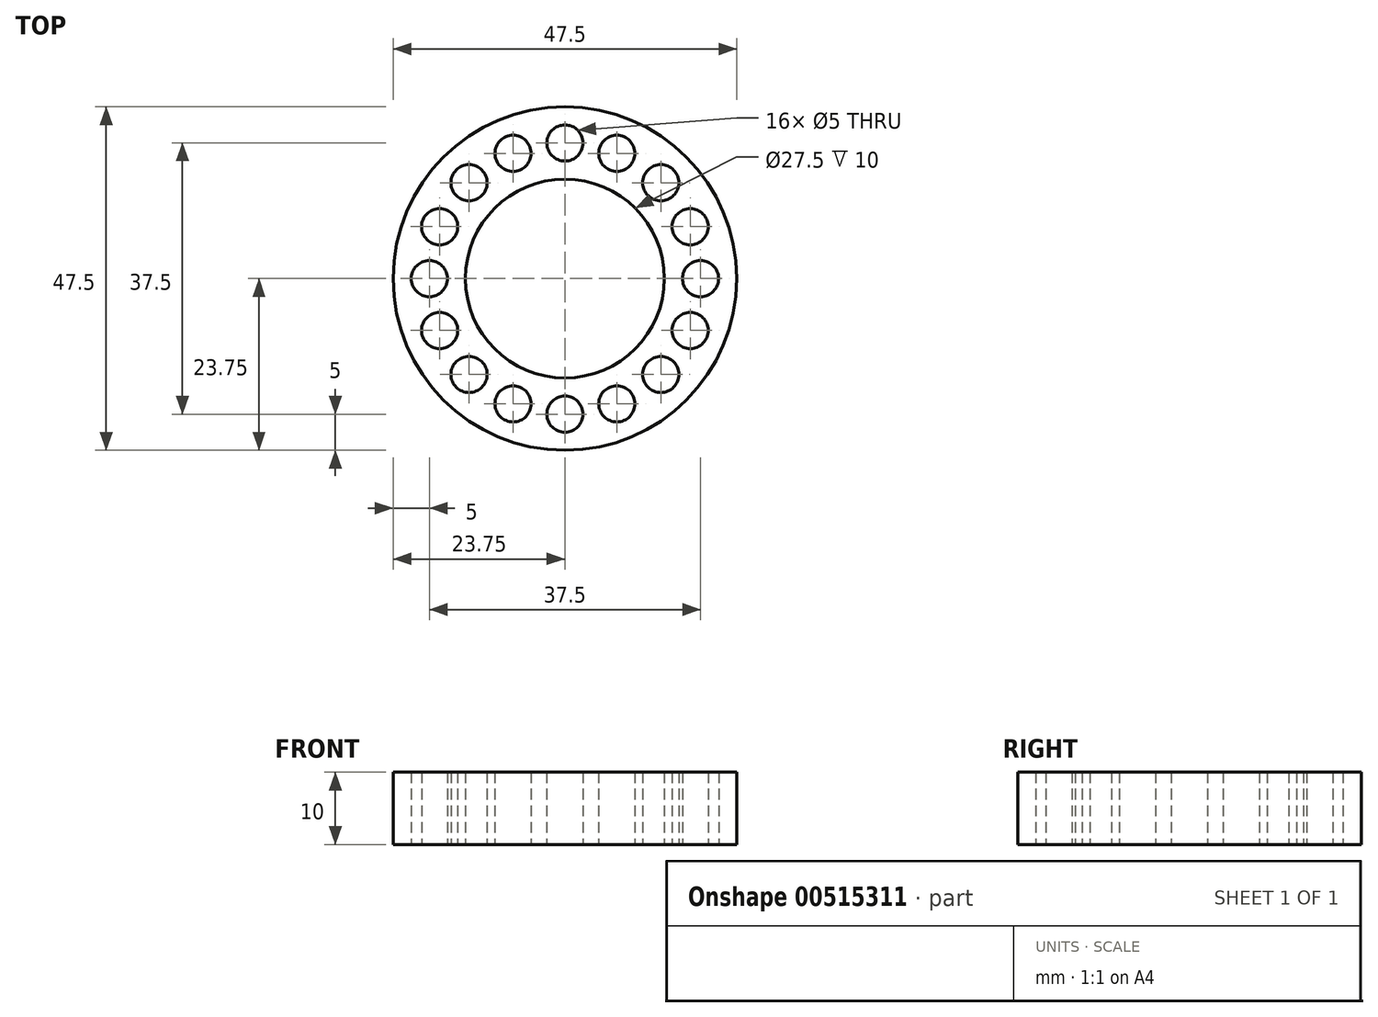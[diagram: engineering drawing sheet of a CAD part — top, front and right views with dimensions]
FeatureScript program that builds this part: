
annotation { "Feature Type Name" : "Feature", "Feature Type Description" : "" }
export const myFeature = defineFeature(function(context is Context, id is Id, definition is map)
    precondition{}
    {
        {
            var Q0;
            Q0=qCreatedBy(makeId("Top.planeOp"),FACE);
            var sketch = newSketch(context, id + "F0", { "sketchPlane" : qUnion([Q0])});
            skCircle(sketch, "E0", {"center": v(0, 0) * mm, "radius": 23.75 * mm});
            skCircle(sketch, "E1", {"center": v(0, 0) * mm, "radius": 13.75 * mm});
            skCircle(sketch, "E2", {"center": v(-13.26, 13.26) * mm, "radius": 2.5 * mm});
            skCircle(sketch, "E3", {"center": v(-18.75, 0) * mm, "radius": 2.5 * mm});
            skCircle(sketch, "E4", {"center": v(-13.26, -13.26) * mm, "radius": 2.5 * mm});
            skCircle(sketch, "E5", {"center": v(0, -18.75) * mm, "radius": 2.5 * mm});
            skCircle(sketch, "E6", {"center": v(13.26, -13.26) * mm, "radius": 2.5 * mm});
            skCircle(sketch, "E7", {"center": v(18.75, 0) * mm, "radius": 2.5 * mm});
            skCircle(sketch, "E8", {"center": v(13.26, 13.26) * mm, "radius": 2.5 * mm});
            skCircle(sketch, "E9", {"center": v(0, 18.75) * mm, "radius": 2.5 * mm});
            skCircle(sketch, "E10", {"center": v(-7.18, 17.32) * mm, "radius": 2.5 * mm});
            skCircle(sketch, "E11", {"center": v(-17.32, 7.18) * mm, "radius": 2.5 * mm});
            skCircle(sketch, "E12", {"center": v(-17.32, -7.18) * mm, "radius": 2.5 * mm});
            skCircle(sketch, "E13", {"center": v(-7.18, -17.32) * mm, "radius": 2.5 * mm});
            skCircle(sketch, "E14", {"center": v(7.18, -17.32) * mm, "radius": 2.5 * mm});
            skCircle(sketch, "E15", {"center": v(17.32, -7.18) * mm, "radius": 2.5 * mm});
            skCircle(sketch, "E16", {"center": v(17.32, 7.18) * mm, "radius": 2.5 * mm});
            skCircle(sketch, "E17", {"center": v(7.18, 17.32) * mm, "radius": 2.5 * mm});
            skSolve(sketch);
        }
        {
            var Q0;
            Q0 = qSketchRegion(id + "F0", true);
            extrude(context, id + "F1", {"entities" : qUnion([Q0]), "depth" : 10 * mm, "offsetDistance" : 25 * mm});
        }
    });
